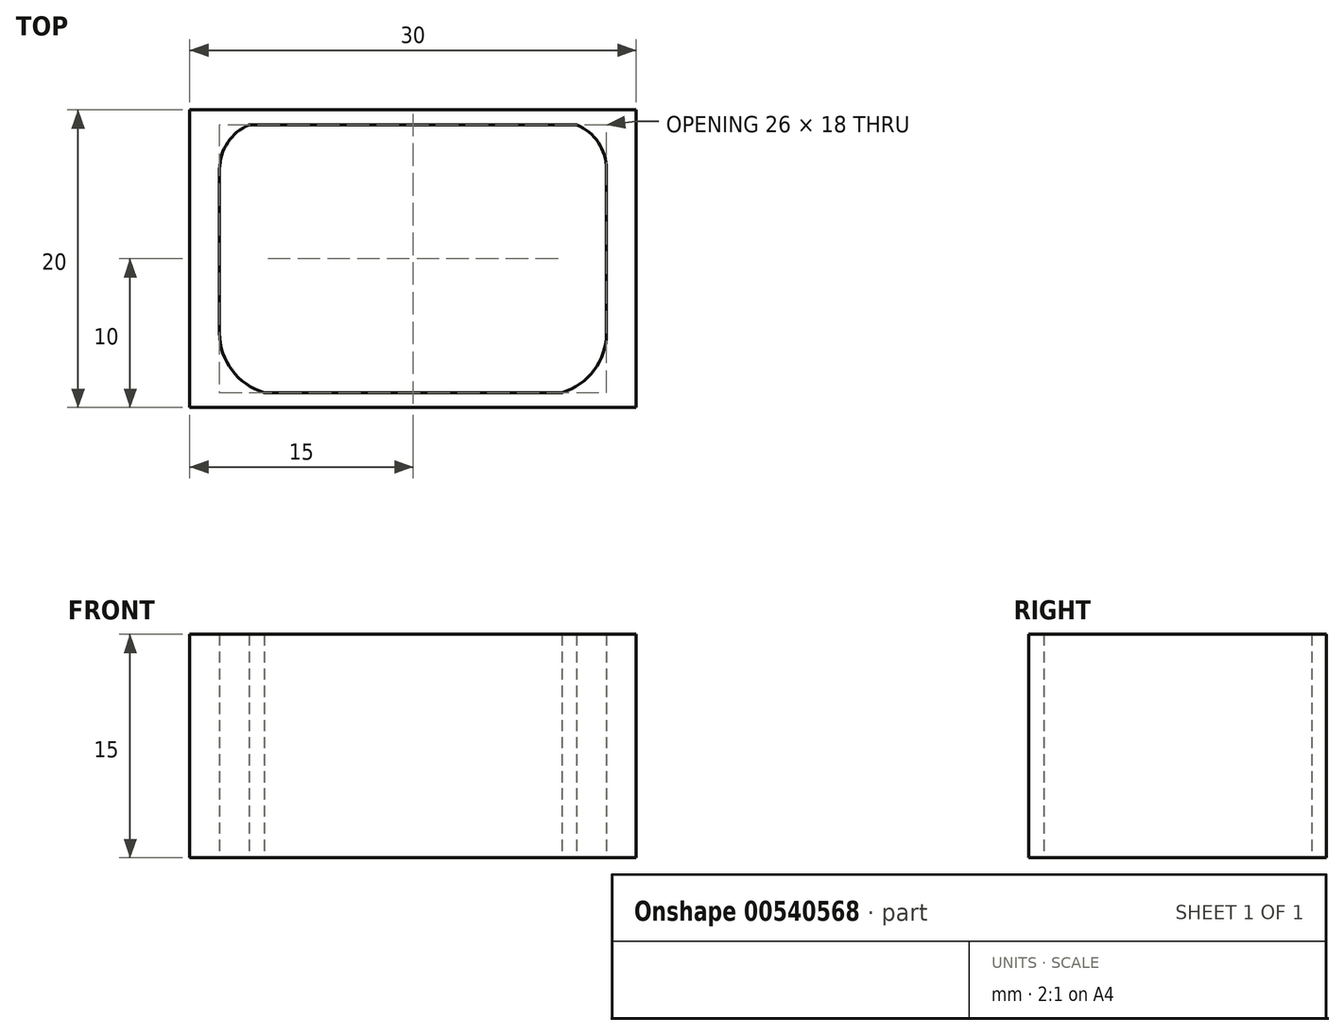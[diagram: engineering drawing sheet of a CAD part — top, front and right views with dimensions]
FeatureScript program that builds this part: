
annotation { "Feature Type Name" : "Feature", "Feature Type Description" : "" }
export const myFeature = defineFeature(function(context is Context, id is Id, definition is map)
    precondition{}
    {
        {
            var Q0;
            Q0=qCreatedBy(makeId("Top.planeOp"),FACE);
            var sketch = newSketch(context, id + "F0", { "sketchPlane" : qUnion([Q0])});
            skLineSegment(sketch, "E0.bottom", {"start": v(15, -10) * mm, "end": v(-15, -10) * mm});
            skLineSegment(sketch, "E0.top", {"start": v(15, 10) * mm, "end": v(-15, 10) * mm});
            skLineSegment(sketch, "E0.left", {"start": v(15, -10) * mm, "end": v(15, 10) * mm});
            skLineSegment(sketch, "E0.right", {"start": v(-15, -10) * mm, "end": v(-15, 10) * mm});
            skPoint(sketch, "E0.middle", {"position": v(0, 0) * mm});
            skLineSegment(sketch, "E1", {"start": v(-13, 6) * mm, "end": v(-13, -5) * mm});
            skLineSegment(sketch, "E2", {"start": v(-11, 9) * mm, "end": v(11, 9) * mm});
            skLineSegment(sketch, "E3", {"start": v(13, 6) * mm, "end": v(13, -5) * mm});
            skLineSegment(sketch, "E4", {"start": v(-10, -9) * mm, "end": v(10, -9) * mm});
            skArc(sketch, "E5", {"start": v(-11, 9) * mm, "mid": v(-12.45, 7.8) * mm, "end": v(-13, 6) * mm});
            skArc(sketch, "E6", {"start": v(13, 6) * mm, "mid": v(12.45, 7.8) * mm, "end": v(11, 9) * mm});
            skArc(sketch, "E7", {"start": v(-13, -5) * mm, "mid": v(-12.17, -7.5) * mm, "end": v(-10, -9) * mm});
            skArc(sketch, "E8", {"start": v(10, -9) * mm, "mid": v(12.17, -7.5) * mm, "end": v(13, -5) * mm});
            skSolve(sketch);
        }
        {
            var Q0;
            Q0 = qSketchRegion(id + "F0", true);
            extrude(context, id + "F1", {"entities" : qUnion([Q0]), "depth" : 15 * mm, "offsetDistance" : 25 * mm});
        }
    });
